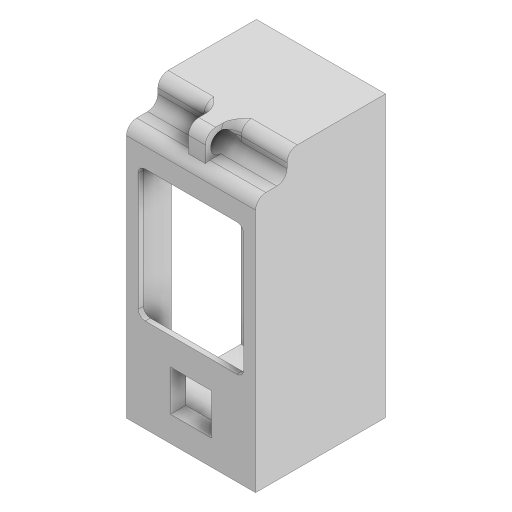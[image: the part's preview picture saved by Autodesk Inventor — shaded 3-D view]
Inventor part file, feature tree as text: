
AUTODESK INVENTOR PART (.ipt)
format: ipt  version: 2023.3 (Build 273359000, 359)  size: 732,672 bytes
history: native  units: mm
features: extrude x20, sketch x19, projected_geometry x6, fillet x4, plane x2, chamfer x1
ambient origin geometry x8: Origin, YZ Plane, XZ Plane, XY Plane, X Axis, Y Axis, Z Axis, Center Point
bodies: Solid1 (feature_tree)
feature tree (52):
  sketch  "Sketch1"  dims[d0=34.0mm d1=45.0mm]
  extrude  "Extrusion1"  Depth=45.0mm
  extrude  "Extrusion2"  Depth=12.0mm
  fillet  "Fillet1"  Radius=12.0mm
  extrude  "Extrusion3"  Depth=58.0mm
  extrude  "Extrusion4"  Depth=13.0mm
  extrude  "Extrusion5"  Depth=3.0mm
  extrude  "Extrusion6"  Depth=3.0mm
  extrude  "Extrusion7"  Depth=3.0mm
  extrude  "Extrusion8"  Depth=3.0mm
  extrude  "Extrusion9"  Depth=2.62mm
  fillet  "Fillet2"  Radius=2.0mm
  extrude  "Extrusion10"  Depth=2.0mm
  chamfer  "Chamfer1"  Distance=4.5mm
  sketch  "Sketch10"  dims[d22=2.0mm d23=2.0mm d24=4.5mm d25=0.0mm]
  extrude  "Extrusion11"  Depth=1.5mm
  extrude  "Extrusion12"  Depth=5.5mm
  extrude  "Extrusion14"  Depth=2.0mm
  extrude  "Extrusion13"  Depth=22.5mm
  sketch  "Sketch13"  dims[d30=1.5mm d31=0.0mm d32=2.0mm]
  extrude  "Extrusion15"  Depth=2.0mm TaperAngle=0.0deg
  extrude  "Extrusion16"  Depth=2.0mm TaperAngle=0.0deg
  extrude  "Extrusion17"  Depth=10.0mm TaperAngle=0.0deg
  extrude  "Extrusion18"  Depth=10.0mm
  extrude  "Extrusion19"  Depth=3.0mm
  fillet  "Fillet4"  Radius=10.0mm
  plane  "Work Plane1"
  sketch  "Sketch18"  dims[d46=10.0mm d47=0.0mm d48=2.15mm]
  plane  "Work Plane3"
  extrude  "Extrusion20"  Depth=3.0mm
  fillet  "Fillet5"  Radius=4.8mm
  sketch  "Sketch2"  dims[d2=2.5mm d3=12.0mm d4=12.0mm]
  sketch  "Sketch3"  dims[d5=34.0mm d6=58.0mm]
  sketch  "Sketch4"  dims[d7=7.0mm d8=13.0mm]
  sketch  "Sketch5"  dims[d9=29.0mm d10=3.0mm]
  sketch  "Sketch6"  dims[d11=3.0mm d12=3.0mm]
  sketch  "Sketch7"  dims[d13=3.0mm d14=28.25mm d15=14.125mm]
  sketch  "Sketch8"  dims[d16=3.0mm d17=24.0mm]
  sketch  "Sketch9"  dims[d18=12.0mm d19=2.62mm d21=2.0mm]
  sketch  "Sketch11"  dims[d26=0.75mm d27=1.5mm]
  sketch  "Sketch12"  dims[d28=1.5mm d29=5.5mm]
  projected_geometry  "Projected Loop1"
  sketch  "Sketch14"  dims[d33=29.25mm d34=0.0mm d35=22.5mm]
  sketch  "Sketch15"  dims[d36=29.25mm d37=0.0mm d38=2.0mm d39=0.0mm]
  projected_geometry  "Projected Loop2"
  sketch  "Sketch16"  dims[d40=7.5mm d41=2.0mm d42=0.0mm]
  projected_geometry  "Projected Loop3"
  sketch  "Sketch17"  dims[d43=2.0mm d44=10.0mm d45=0.0mm]
  projected_geometry  "Projected Loop4"
  projected_geometry  "Projected Loop5"
  projected_geometry  "Projected Loop6"
  sketch  "Sketch20"  dims[d49=3.6mm d50=9.25mm d51=10.0mm d52=0.0mm d53=0.75mm d54=4.8mm d55=39.25mm d56=10.65mm d57=1.0mm d58=3.0mm d59=0.0mm d61=2.0mm d62=2.0mm d63=45.0deg d64=3.732763mm d65=3.732763mm d66=4.8mm d67=4.8mm d68=4.8mm d69=4.8mm d70=3.0mm d71=0.0mm d72=5.8mm d73=2.7mm d74=1.0mm d75=5.5mm d76=10.0mm d77=0.0mm d78=5.5mm d79=10.0mm d80=0.0mm d81=5.8mm d82=2.7mm d83=1.0mm d85=5.5mm d86=5.8mm d87=2.7mm d88=1.0mm d89=10.0mm d90=0.0mm d91=10.0mm d92=0.0mm d93=10.0mm d94=0.0mm d95=3.2mm d96=3.2mm d97=10.0mm d98=0.0mm d99=6.4mm d100=6.4mm d101=2.5mm d102=0.0mm d103=1.5mm d104=0.0mm d105=3.0mm d106=16.072818mm d107=16.072818mm d108=6.0mm d109=7.5mm d110=6.0mm d112=5.0mm d113=0.0mm d114=3.0mm]
